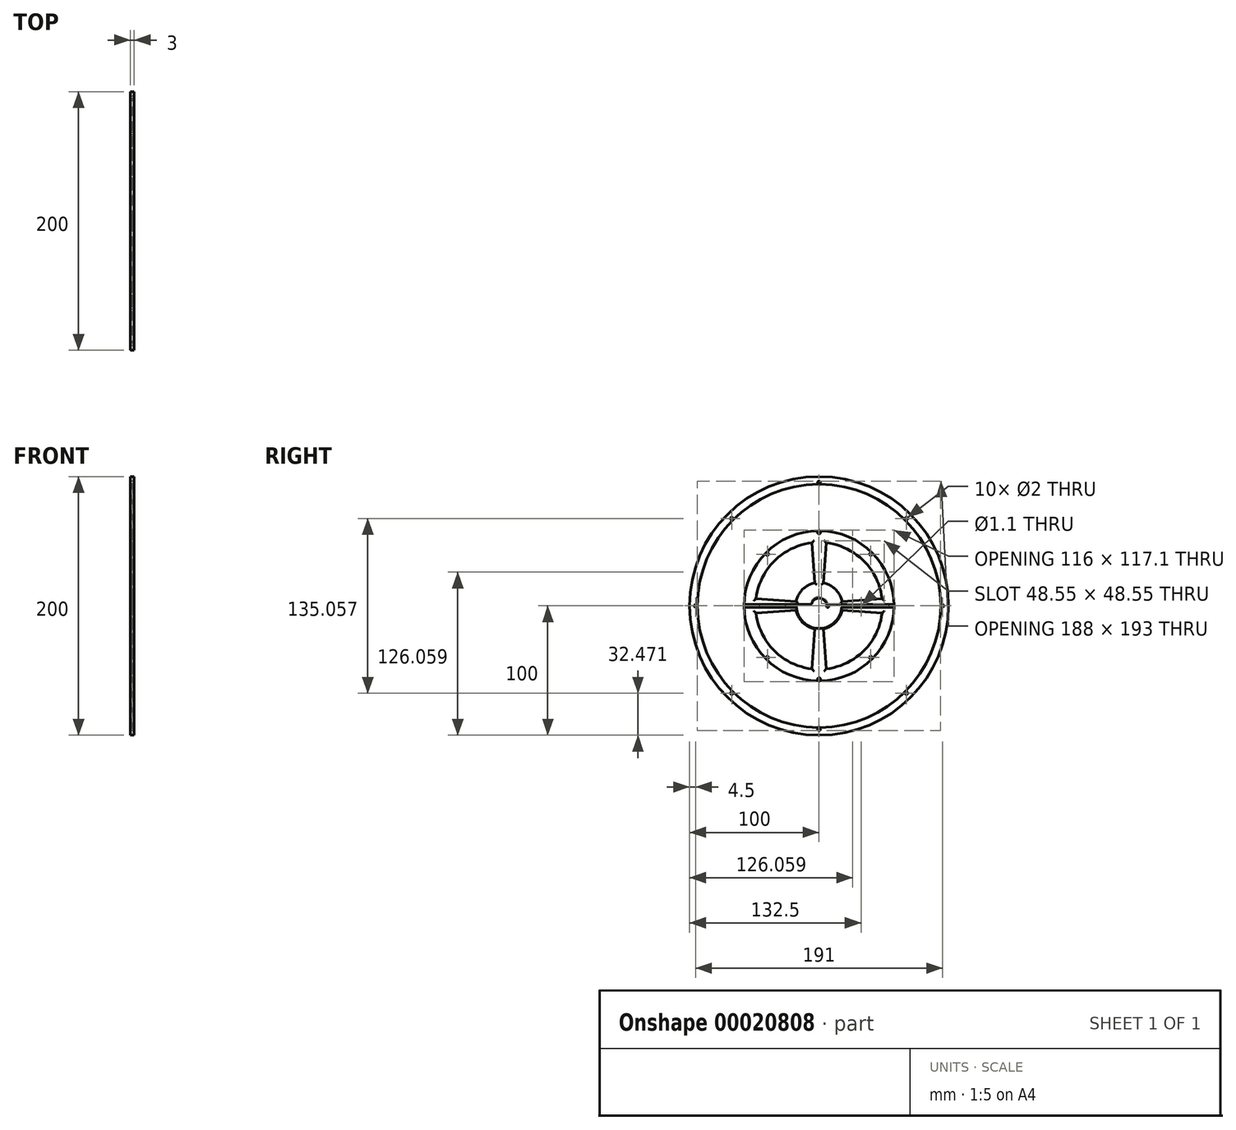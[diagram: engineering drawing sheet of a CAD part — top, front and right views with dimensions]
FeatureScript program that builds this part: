
annotation { "Feature Type Name" : "Feature", "Feature Type Description" : "" }
export const myFeature = defineFeature(function(context is Context, id is Id, definition is map)
    precondition{}
    {
        {
            var Q0;
            Q0=qCreatedBy(makeId("Right.planeOp"),FACE);
            var sketch = newSketch(context, id + "F0", { "sketchPlane" : qUnion([Q0])});
            skCircle(sketch, "E0", {"center": v(0, 0) * mm, "radius": 49 * mm});
            skCircle(sketch, "E1", {"center": v(0, 0) * mm, "radius": 58 * mm});
            skCircle(sketch, "E2", {"center": v(0, 0) * mm, "radius": 94 * mm});
            skCircle(sketch, "E3", {"center": v(0, 0) * mm, "radius": 100 * mm});
            skCircle(sketch, "E4", {"center": v(0, 0) * mm, "radius": 18 * mm});
            skCircle(sketch, "E5", {"center": v(0, 0) * mm, "radius": 6 * mm});
            skCircle(sketch, "E6", {"center": v(0, 0) * mm, "radius": 6.5 * mm});
            skCircle(sketch, "E7", {"center": v(0, 0) * mm, "radius": 7 * mm});
            skCircle(sketch, "E8.cCircle", {"center": v(0, 0) * mm, "radius": 58 * mm, "construction": true});
            skCircle(sketch, "E9", {"center": v(56.5, 0) * mm, "radius": 1 * mm});
            skCircle(sketch, "E10", {"center": v(95.5, 0) * mm, "radius": 1 * mm});
            skCircle(sketch, "E11.1.0", {"center": v(67.53, 67.53) * mm, "radius": 1 * mm});
            skCircle(sketch, "E11.1.1", {"center": v(39.95, 39.95) * mm, "radius": 1 * mm});
            skCircle(sketch, "E11.2.0", {"center": v(0, 95.5) * mm, "radius": 1 * mm});
            skCircle(sketch, "E11.2.1", {"center": v(0, 56.5) * mm, "radius": 1 * mm});
            skCircle(sketch, "E12.1.3.0", {"center": v(-67.53, 67.53) * mm, "radius": 1 * mm});
            skCircle(sketch, "E12.2.3.0", {"center": v(-39.95, 39.95) * mm, "radius": 1 * mm});
            skCircle(sketch, "E12.1.4.0", {"center": v(-95.5, 0) * mm, "radius": 1 * mm});
            skCircle(sketch, "E12.2.4.0", {"center": v(-56.5, 0) * mm, "radius": 1 * mm});
            skCircle(sketch, "E12.1.5.0", {"center": v(-67.53, -67.53) * mm, "radius": 1 * mm});
            skCircle(sketch, "E12.2.5.0", {"center": v(-39.95, -39.95) * mm, "radius": 1 * mm});
            skCircle(sketch, "E12.1.6.0", {"center": v(0, -95.5) * mm, "radius": 1 * mm});
            skCircle(sketch, "E12.2.6.0", {"center": v(0, -56.5) * mm, "radius": 1 * mm});
            skCircle(sketch, "E12.1.7.0", {"center": v(67.53, -67.53) * mm, "radius": 1 * mm});
            skCircle(sketch, "E12.2.7.0", {"center": v(39.95, -39.95) * mm, "radius": 1 * mm});
            skPoint(sketch, "E13", {"position": v(0, -58) * mm});
            skPoint(sketch, "E14", {"position": v(0, -94) * mm});
            skPoint(sketch, "E15", {"position": v(18.53, 0) * mm});
            skPoint(sketch, "E16", {"position": v(32.5, 0) * mm});
            skPoint(sketch, "E17", {"position": v(-17.5, 0) * mm});
            skPoint(sketch, "E18", {"position": v(-7.5, 0) * mm});
            skPoint(sketch, "E19", {"position": v(55, 0) * mm});
            skPoint(sketch, "E20", {"position": v(-55, 0) * mm});
            skLineSegment(sketch, "E21.rect.bottom", {"start": v(56.5, -1) * mm, "end": v(-56.5, -1) * mm});
            skLineSegment(sketch, "E21.rect.top", {"start": v(56.5, 1) * mm, "end": v(-56.5, 1) * mm});
            skLineSegment(sketch, "E21.rect.left", {"start": v(56.5, -1) * mm, "end": v(56.5, 1) * mm});
            skLineSegment(sketch, "E21.rect.right", {"start": v(-56.5, -1) * mm, "end": v(-56.5, 1) * mm});
            skPoint(sketch, "E22", {"position": v(0, 94) * mm});
            skPoint(sketch, "E23", {"position": v(0, 58) * mm});
            skCircle(sketch, "E24", {"center": v(0, 0) * mm, "radius": 56.5 * mm});
            skCircle(sketch, "E25", {"center": v(0, 0) * mm, "radius": 7.5 * mm});
            skCircle(sketch, "E26", {"center": v(0, 0) * mm, "radius": 17.5 * mm});
            skCircle(sketch, "E27", {"center": v(0, 0) * mm, "radius": 55 * mm});
            skPoint(sketch, "E28.0.midPoint", {"position": v(-58, 0) * mm});
            skLineSegment(sketch, "E29", {"start": v(5.48, 48.7) * mm, "end": v(3.37, 17.68) * mm});
            skLineSegment(sketch, "E30", {"start": v(-5.48, 48.7) * mm, "end": v(-3.37, 17.68) * mm});
            skLineSegment(sketch, "E31", {"start": v(48.7, -5.48) * mm, "end": v(17.68, -3.37) * mm});
            skLineSegment(sketch, "E32", {"start": v(48.7, 5.48) * mm, "end": v(17.68, 3.37) * mm});
            skLineSegment(sketch, "E33", {"start": v(-48.7, -5.48) * mm, "end": v(-17.68, -3.37) * mm});
            skLineSegment(sketch, "E34", {"start": v(-48.7, 5.48) * mm, "end": v(-17.68, 3.37) * mm});
            skLineSegment(sketch, "E35", {"start": v(-5.48, -48.7) * mm, "end": v(-3.37, -17.68) * mm});
            skLineSegment(sketch, "E36", {"start": v(3.37, -17.68) * mm, "end": v(5.48, -48.7) * mm});
            skSolve(sketch);
        }
        {
            var Q0;
            Q0=makeQuery(id+"F0.imprint","IMPRINT",FACE,{"disambiguationData":[TD([[makeQuery(id+"F0.imprint","IMPRINT",EDGE,{"derivedFrom":sQuery(id+"F0.wireOp",EDGE,"E2")}),-1.0]])]});
            var Q1;
            Q1=makeQuery(id+"F0.imprint","IMPRINT",FACE,{"disambiguationData":[TD([[makeQuery(id+"F0.imprint","IMPRINT",EDGE,{"derivedFrom":sQuery(id+"F0.wireOp",EDGE,"E1")}),1.0]])]});
            var Q2;
            {var subQ4=sQuery(id+"F0.wireOp",EDGE,"E24");var subQ12=sQuery(id+"F0.wireOp",EDGE,"E11.1.1");var subQ14=makeQuery(id+"F0.imprint","INTERSECT",VERTEX,{"disambiguationData":[OD(0.0)],"derivedFrom":[subQ12,subQ4]});Q2=makeQuery(id+"F0.imprint","IMPRINT",FACE,{"disambiguationData":[TD([[makeQuery(id+"F0.imprint","IMPRINT",EDGE,{"disambiguationData":[TD([[subQ14,1.0]])],"derivedFrom":subQ12}),-1.0]])]});}
            var Q3;
            {var subQ4=sQuery(id+"F0.wireOp",EDGE,"E0");var subQ10=makeQuery(id+"F0.imprint","INTERSECT",VERTEX,{"derivedFrom":[subQ4,sQuery(id+"F0.wireOp",EDGE,"E32")]});Q3=makeQuery(id+"F0.imprint","IMPRINT",FACE,{"disambiguationData":[TD([[makeQuery(id+"F0.imprint","IMPRINT",EDGE,{"disambiguationData":[TD([[subQ10,1.0]])],"derivedFrom":subQ4}),-1.0]])]});}
            var Q4;
            {var subQ4=sQuery(id+"F0.wireOp",EDGE,"E0");var subQ10=makeQuery(id+"F0.imprint","INTERSECT",VERTEX,{"derivedFrom":[subQ4,sQuery(id+"F0.wireOp",EDGE,"E33")]});Q4=makeQuery(id+"F0.imprint","IMPRINT",FACE,{"disambiguationData":[TD([[makeQuery(id+"F0.imprint","IMPRINT",EDGE,{"disambiguationData":[TD([[subQ10,1.0]])],"derivedFrom":subQ4}),-1.0]])]});}
            var Q5;
            {var subQ0=sQuery(id+"F0.wireOp",EDGE,"E34");Q5=makeQuery(id+"F0.imprint","IMPRINT",FACE,{"disambiguationData":[TD([[makeQuery(id+"F0.imprint","IMPRINT",EDGE,{"derivedFrom":subQ0}),-1.0]])]});}
            var Q6;
            {var subQ0=sQuery(id+"F0.wireOp",EDGE,"E33");Q6=makeQuery(id+"F0.imprint","IMPRINT",FACE,{"disambiguationData":[TD([[makeQuery(id+"F0.imprint","IMPRINT",EDGE,{"derivedFrom":subQ0}),1.0]])]});}
            var Q7;
            {var subQ0=sQuery(id+"F0.wireOp",EDGE,"E26");var subQ1=sQuery(id+"F0.wireOp",EDGE,"E21.rect.top");var subQ3=makeQuery(id+"F0.imprint","INTERSECT",VERTEX,{"disambiguationData":[OD(0.0)],"derivedFrom":[subQ1,subQ0]});Q7=makeQuery(id+"F0.imprint","IMPRINT",FACE,{"disambiguationData":[TD([[makeQuery(id+"F0.imprint","IMPRINT",EDGE,{"disambiguationData":[TD([[subQ3,-1.0]])],"derivedFrom":subQ1}),-1.0]])]});}
            var Q8;
            {var subQ1=sQuery(id+"F0.wireOp",EDGE,"E29");Q8=makeQuery(id+"F0.imprint","IMPRINT",FACE,{"disambiguationData":[TD([[makeQuery(id+"F0.imprint","IMPRINT",EDGE,{"derivedFrom":subQ1}),-1.0]])]});}
            var Q9;
            {var subQ0=sQuery(id+"F0.wireOp",EDGE,"E32");Q9=makeQuery(id+"F0.imprint","IMPRINT",FACE,{"disambiguationData":[TD([[makeQuery(id+"F0.imprint","IMPRINT",EDGE,{"derivedFrom":subQ0}),1.0]])]});}
            var Q10;
            {var subQ0=sQuery(id+"F0.wireOp",EDGE,"E31");Q10=makeQuery(id+"F0.imprint","IMPRINT",FACE,{"disambiguationData":[TD([[makeQuery(id+"F0.imprint","IMPRINT",EDGE,{"derivedFrom":subQ0}),-1.0]])]});}
            var Q11;
            {var subQ0=sQuery(id+"F0.wireOp",EDGE,"E26");var subQ1=sQuery(id+"F0.wireOp",EDGE,"E21.rect.bottom");var subQ3=makeQuery(id+"F0.imprint","INTERSECT",VERTEX,{"disambiguationData":[OD(0.0)],"derivedFrom":[subQ1,subQ0]});Q11=makeQuery(id+"F0.imprint","IMPRINT",FACE,{"disambiguationData":[TD([[makeQuery(id+"F0.imprint","IMPRINT",EDGE,{"disambiguationData":[TD([[subQ3,-1.0]])],"derivedFrom":subQ1}),1.0]])]});}
            var Q12;
            {var subQ1=sQuery(id+"F0.wireOp",EDGE,"E35");Q12=makeQuery(id+"F0.imprint","IMPRINT",FACE,{"disambiguationData":[TD([[makeQuery(id+"F0.imprint","IMPRINT",EDGE,{"derivedFrom":subQ1}),-1.0]])]});}
            var Q13;
            {var subQ0=sQuery(id+"F0.wireOp",EDGE,"E24");var subQ10=sQuery(id+"F0.wireOp",EDGE,"E12.2.5.0");var subQ12=makeQuery(id+"F0.imprint","INTERSECT",VERTEX,{"disambiguationData":[OD(0.0)],"derivedFrom":[subQ10,subQ0]});Q13=makeQuery(id+"F0.imprint","IMPRINT",FACE,{"disambiguationData":[TD([[makeQuery(id+"F0.imprint","IMPRINT",EDGE,{"disambiguationData":[TD([[subQ12,1.0]])],"derivedFrom":subQ10}),-1.0]])]});}
            var Q14;
            {var subQ3=sQuery(id+"F0.wireOp",EDGE,"E4");var subQ10=makeQuery(id+"F0.imprint","INTERSECT",VERTEX,{"derivedFrom":[subQ3,sQuery(id+"F0.wireOp",EDGE,"E33")]});Q14=makeQuery(id+"F0.imprint","IMPRINT",FACE,{"disambiguationData":[TD([[makeQuery(id+"F0.imprint","IMPRINT",EDGE,{"disambiguationData":[TD([[subQ10,1.0]])],"derivedFrom":subQ3}),1.0]])]});}
            var Q15;
            {var subQ1=sQuery(id+"F0.wireOp",EDGE,"E21.rect.bottom");var subQ4=sQuery(id+"F0.wireOp",EDGE,"E7");var subQ5=makeQuery(id+"F0.imprint","INTERSECT",VERTEX,{"disambiguationData":[OD(0.0)],"derivedFrom":[subQ4,subQ1]});Q15=makeQuery(id+"F0.imprint","IMPRINT",FACE,{"disambiguationData":[TD([[makeQuery(id+"F0.imprint","IMPRINT",EDGE,{"disambiguationData":[TD([[subQ5,-1.0]])],"derivedFrom":subQ4}),-1.0]])]});}
            var Q16;
            {var subQ0=sQuery(id+"F0.wireOp",EDGE,"E21.rect.bottom");var subQ3=sQuery(id+"F0.wireOp",EDGE,"E6");var subQ4=makeQuery(id+"F0.imprint","INTERSECT",VERTEX,{"disambiguationData":[OD(0.0)],"derivedFrom":[subQ3,subQ0]});Q16=makeQuery(id+"F0.imprint","IMPRINT",FACE,{"disambiguationData":[TD([[makeQuery(id+"F0.imprint","IMPRINT",EDGE,{"disambiguationData":[TD([[subQ4,-1.0]])],"derivedFrom":subQ3}),-1.0]])]});}
            var Q17;
            {var subQ0=sQuery(id+"F0.wireOp",EDGE,"E21.rect.bottom");var subQ3=sQuery(id+"F0.wireOp",EDGE,"E5");var subQ4=makeQuery(id+"F0.imprint","INTERSECT",VERTEX,{"disambiguationData":[OD(0.0)],"derivedFrom":[subQ3,subQ0]});Q17=makeQuery(id+"F0.imprint","IMPRINT",FACE,{"disambiguationData":[TD([[makeQuery(id+"F0.imprint","IMPRINT",EDGE,{"disambiguationData":[TD([[subQ4,-1.0]])],"derivedFrom":subQ3}),-1.0]])]});}
            var Q18;
            {var subQ1=sQuery(id+"F0.wireOp",EDGE,"E21.rect.top");var subQ5=sQuery(id+"F0.wireOp",EDGE,"E7");var subQ6=makeQuery(id+"F0.imprint","INTERSECT",VERTEX,{"disambiguationData":[OD(0.0)],"derivedFrom":[subQ5,subQ1]});Q18=makeQuery(id+"F0.imprint","IMPRINT",FACE,{"disambiguationData":[TD([[makeQuery(id+"F0.imprint","IMPRINT",EDGE,{"disambiguationData":[TD([[subQ6,-1.0]])],"derivedFrom":subQ5}),-1.0]])]});}
            var Q19;
            {var subQ0=sQuery(id+"F0.wireOp",EDGE,"E21.rect.top");var subQ3=sQuery(id+"F0.wireOp",EDGE,"E6");var subQ4=makeQuery(id+"F0.imprint","INTERSECT",VERTEX,{"disambiguationData":[OD(0.0)],"derivedFrom":[subQ3,subQ0]});Q19=makeQuery(id+"F0.imprint","IMPRINT",FACE,{"disambiguationData":[TD([[makeQuery(id+"F0.imprint","IMPRINT",EDGE,{"disambiguationData":[TD([[subQ4,-1.0]])],"derivedFrom":subQ3}),-1.0]])]});}
            var Q20;
            {var subQ0=sQuery(id+"F0.wireOp",EDGE,"E21.rect.top");var subQ3=sQuery(id+"F0.wireOp",EDGE,"E5");var subQ4=makeQuery(id+"F0.imprint","INTERSECT",VERTEX,{"disambiguationData":[OD(0.0)],"derivedFrom":[subQ3,subQ0]});Q20=makeQuery(id+"F0.imprint","IMPRINT",FACE,{"disambiguationData":[TD([[makeQuery(id+"F0.imprint","IMPRINT",EDGE,{"disambiguationData":[TD([[subQ4,-1.0]])],"derivedFrom":subQ3}),-1.0]])]});}
            var Q21;
            {var subQ3=sQuery(id+"F0.wireOp",EDGE,"E5");var subQ5=sQuery(id+"F0.wireOp",EDGE,"E21.rect.top");var subQ7=makeQuery(id+"F0.imprint","INTERSECT",VERTEX,{"disambiguationData":[OD(1.0)],"derivedFrom":[subQ3,subQ5]});Q21=makeQuery(id+"F0.imprint","IMPRINT",FACE,{"disambiguationData":[TD([[makeQuery(id+"F0.imprint","IMPRINT",EDGE,{"disambiguationData":[TD([[subQ7,1.0]])],"derivedFrom":subQ3}),-1.0]])]});}
            var Q22;
            {var subQ0=sQuery(id+"F0.wireOp",EDGE,"E21.rect.top");var subQ3=sQuery(id+"F0.wireOp",EDGE,"E6");var subQ4=makeQuery(id+"F0.imprint","INTERSECT",VERTEX,{"disambiguationData":[OD(1.0)],"derivedFrom":[subQ3,subQ0]});Q22=makeQuery(id+"F0.imprint","IMPRINT",FACE,{"disambiguationData":[TD([[makeQuery(id+"F0.imprint","IMPRINT",EDGE,{"disambiguationData":[TD([[subQ4,1.0]])],"derivedFrom":subQ3}),-1.0]])]});}
            var Q23;
            {var subQ1=sQuery(id+"F0.wireOp",EDGE,"E21.rect.top");var subQ5=sQuery(id+"F0.wireOp",EDGE,"E7");var subQ6=makeQuery(id+"F0.imprint","INTERSECT",VERTEX,{"disambiguationData":[OD(1.0)],"derivedFrom":[subQ5,subQ1]});Q23=makeQuery(id+"F0.imprint","IMPRINT",FACE,{"disambiguationData":[TD([[makeQuery(id+"F0.imprint","IMPRINT",EDGE,{"disambiguationData":[TD([[subQ6,1.0]])],"derivedFrom":subQ5}),-1.0]])]});}
            var Q24;
            {var subQ1=sQuery(id+"F0.wireOp",EDGE,"E21.rect.top");var subQ4=sQuery(id+"F0.wireOp",EDGE,"E7");var subQ5=makeQuery(id+"F0.imprint","INTERSECT",VERTEX,{"disambiguationData":[OD(0.0)],"derivedFrom":[subQ4,subQ1]});Q24=makeQuery(id+"F0.imprint","IMPRINT",FACE,{"disambiguationData":[TD([[makeQuery(id+"F0.imprint","IMPRINT",EDGE,{"disambiguationData":[TD([[subQ5,1.0]])],"derivedFrom":subQ4}),-1.0]])]});}
            var Q25;
            {var subQ0=sQuery(id+"F0.wireOp",EDGE,"E21.rect.top");var subQ3=sQuery(id+"F0.wireOp",EDGE,"E6");var subQ4=makeQuery(id+"F0.imprint","INTERSECT",VERTEX,{"disambiguationData":[OD(0.0)],"derivedFrom":[subQ3,subQ0]});Q25=makeQuery(id+"F0.imprint","IMPRINT",FACE,{"disambiguationData":[TD([[makeQuery(id+"F0.imprint","IMPRINT",EDGE,{"disambiguationData":[TD([[subQ4,1.0]])],"derivedFrom":subQ3}),-1.0]])]});}
            var Q26;
            {var subQ0=sQuery(id+"F0.wireOp",EDGE,"E21.rect.top");var subQ3=sQuery(id+"F0.wireOp",EDGE,"E5");var subQ4=makeQuery(id+"F0.imprint","INTERSECT",VERTEX,{"disambiguationData":[OD(0.0)],"derivedFrom":[subQ3,subQ0]});Q26=makeQuery(id+"F0.imprint","IMPRINT",FACE,{"disambiguationData":[TD([[makeQuery(id+"F0.imprint","IMPRINT",EDGE,{"disambiguationData":[TD([[subQ4,1.0]])],"derivedFrom":subQ3}),-1.0]])]});}
            var Q27;
            {var subQ3=sQuery(id+"F0.wireOp",EDGE,"E4");var subQ10=makeQuery(id+"F0.imprint","INTERSECT",VERTEX,{"derivedFrom":[subQ3,sQuery(id+"F0.wireOp",EDGE,"E32")]});Q27=makeQuery(id+"F0.imprint","IMPRINT",FACE,{"disambiguationData":[TD([[makeQuery(id+"F0.imprint","IMPRINT",EDGE,{"disambiguationData":[TD([[subQ10,1.0]])],"derivedFrom":subQ3}),1.0]])]});}
            extrude(context, id + "F1", {"entities" : qUnion([Q0, Q1, Q2, Q3, Q4, Q5, Q6, Q7, Q8, Q9, Q10, Q11, Q12, Q13, Q14, Q15, Q16, Q17, Q18, Q19, Q20, Q21, Q22, Q23, Q24, Q25, Q26, Q27]), "depth" : 1 * mm});
        }
        {
            var Q0;
            Q0=makeQuery(id+"F0.imprint","IMPRINT",FACE,{"disambiguationData":[TD([[makeQuery(id+"F0.imprint","IMPRINT",EDGE,{"derivedFrom":sQuery(id+"F0.wireOp",EDGE,"E2")}),-1.0]])]});
            var Q1;
            Q1=makeQuery(id+"F0.imprint","IMPRINT",FACE,{"disambiguationData":[TD([[makeQuery(id+"F0.imprint","IMPRINT",EDGE,{"derivedFrom":sQuery(id+"F0.wireOp",EDGE,"E1")}),-1.0]])]});
            var Q2;
            Q2=makeQuery(id+"F0.imprint","IMPRINT",FACE,{"disambiguationData":[TD([[makeQuery(id+"F0.imprint","IMPRINT",EDGE,{"derivedFrom":sQuery(id+"F0.wireOp",EDGE,"E1")}),1.0]])]});
            var Q3;
            {var subQ4=sQuery(id+"F0.wireOp",EDGE,"E24");var subQ12=sQuery(id+"F0.wireOp",EDGE,"E11.1.1");var subQ14=makeQuery(id+"F0.imprint","INTERSECT",VERTEX,{"disambiguationData":[OD(0.0)],"derivedFrom":[subQ12,subQ4]});Q3=makeQuery(id+"F0.imprint","IMPRINT",FACE,{"disambiguationData":[TD([[makeQuery(id+"F0.imprint","IMPRINT",EDGE,{"disambiguationData":[TD([[subQ14,1.0]])],"derivedFrom":subQ12}),-1.0]])]});}
            var Q4;
            {var subQ4=sQuery(id+"F0.wireOp",EDGE,"E0");var subQ10=makeQuery(id+"F0.imprint","INTERSECT",VERTEX,{"derivedFrom":[subQ4,sQuery(id+"F0.wireOp",EDGE,"E32")]});Q4=makeQuery(id+"F0.imprint","IMPRINT",FACE,{"disambiguationData":[TD([[makeQuery(id+"F0.imprint","IMPRINT",EDGE,{"disambiguationData":[TD([[subQ10,1.0]])],"derivedFrom":subQ4}),-1.0]])]});}
            var Q5;
            {var subQ4=sQuery(id+"F0.wireOp",EDGE,"E0");var subQ10=makeQuery(id+"F0.imprint","INTERSECT",VERTEX,{"derivedFrom":[subQ4,sQuery(id+"F0.wireOp",EDGE,"E33")]});Q5=makeQuery(id+"F0.imprint","IMPRINT",FACE,{"disambiguationData":[TD([[makeQuery(id+"F0.imprint","IMPRINT",EDGE,{"disambiguationData":[TD([[subQ10,1.0]])],"derivedFrom":subQ4}),-1.0]])]});}
            var Q6;
            {var subQ0=sQuery(id+"F0.wireOp",EDGE,"E24");var subQ10=sQuery(id+"F0.wireOp",EDGE,"E12.2.5.0");var subQ12=makeQuery(id+"F0.imprint","INTERSECT",VERTEX,{"disambiguationData":[OD(0.0)],"derivedFrom":[subQ10,subQ0]});Q6=makeQuery(id+"F0.imprint","IMPRINT",FACE,{"disambiguationData":[TD([[makeQuery(id+"F0.imprint","IMPRINT",EDGE,{"disambiguationData":[TD([[subQ12,1.0]])],"derivedFrom":subQ10}),-1.0]])]});}
            var Q7;
            {var subQ1=sQuery(id+"F0.wireOp",EDGE,"E21.rect.top");var subQ5=sQuery(id+"F0.wireOp",EDGE,"E0");var subQ6=makeQuery(id+"F0.imprint","INTERSECT",VERTEX,{"disambiguationData":[OD(1.0)],"derivedFrom":[subQ5,subQ1]});Q7=makeQuery(id+"F0.imprint","IMPRINT",FACE,{"disambiguationData":[TD([[makeQuery(id+"F0.imprint","IMPRINT",EDGE,{"disambiguationData":[TD([[subQ6,-1.0]])],"derivedFrom":subQ5}),-1.0]])]});}
            var Q8;
            {var subQ0=sQuery(id+"F0.wireOp",EDGE,"E34");Q8=makeQuery(id+"F0.imprint","IMPRINT",FACE,{"disambiguationData":[TD([[makeQuery(id+"F0.imprint","IMPRINT",EDGE,{"derivedFrom":subQ0}),-1.0]])]});}
            var Q9;
            {var subQ0=sQuery(id+"F0.wireOp",EDGE,"E33");Q9=makeQuery(id+"F0.imprint","IMPRINT",FACE,{"disambiguationData":[TD([[makeQuery(id+"F0.imprint","IMPRINT",EDGE,{"derivedFrom":subQ0}),1.0]])]});}
            var Q10;
            {var subQ0=sQuery(id+"F0.wireOp",EDGE,"E26");var subQ1=sQuery(id+"F0.wireOp",EDGE,"E21.rect.top");var subQ3=makeQuery(id+"F0.imprint","INTERSECT",VERTEX,{"disambiguationData":[OD(0.0)],"derivedFrom":[subQ1,subQ0]});Q10=makeQuery(id+"F0.imprint","IMPRINT",FACE,{"disambiguationData":[TD([[makeQuery(id+"F0.imprint","IMPRINT",EDGE,{"disambiguationData":[TD([[subQ3,-1.0]])],"derivedFrom":subQ1}),-1.0]])]});}
            var Q11;
            {var subQ0=sQuery(id+"F0.wireOp",EDGE,"E26");var subQ1=sQuery(id+"F0.wireOp",EDGE,"E21.rect.bottom");var subQ3=makeQuery(id+"F0.imprint","INTERSECT",VERTEX,{"disambiguationData":[OD(0.0)],"derivedFrom":[subQ1,subQ0]});Q11=makeQuery(id+"F0.imprint","IMPRINT",FACE,{"disambiguationData":[TD([[makeQuery(id+"F0.imprint","IMPRINT",EDGE,{"disambiguationData":[TD([[subQ3,-1.0]])],"derivedFrom":subQ1}),1.0]])]});}
            var Q12;
            {var subQ1=sQuery(id+"F0.wireOp",EDGE,"E29");Q12=makeQuery(id+"F0.imprint","IMPRINT",FACE,{"disambiguationData":[TD([[makeQuery(id+"F0.imprint","IMPRINT",EDGE,{"derivedFrom":subQ1}),-1.0]])]});}
            var Q13;
            {var subQ0=sQuery(id+"F0.wireOp",EDGE,"E21.rect.top");var subQ3=sQuery(id+"F0.wireOp",EDGE,"E0");var subQ4=makeQuery(id+"F0.imprint","INTERSECT",VERTEX,{"disambiguationData":[OD(0.0)],"derivedFrom":[subQ3,subQ0]});Q13=makeQuery(id+"F0.imprint","IMPRINT",FACE,{"disambiguationData":[TD([[makeQuery(id+"F0.imprint","IMPRINT",EDGE,{"disambiguationData":[TD([[subQ4,1.0]])],"derivedFrom":subQ3}),1.0]])]});}
            var Q14;
            {var subQ0=sQuery(id+"F0.wireOp",EDGE,"E31");Q14=makeQuery(id+"F0.imprint","IMPRINT",FACE,{"disambiguationData":[TD([[makeQuery(id+"F0.imprint","IMPRINT",EDGE,{"derivedFrom":subQ0}),-1.0]])]});}
            var Q15;
            {var subQ0=sQuery(id+"F0.wireOp",EDGE,"E26");var subQ3=sQuery(id+"F0.wireOp",EDGE,"E21.rect.bottom");var subQ4=makeQuery(id+"F0.imprint","INTERSECT",VERTEX,{"disambiguationData":[OD(0.0)],"derivedFrom":[subQ3,subQ0]});Q15=makeQuery(id+"F0.imprint","IMPRINT",FACE,{"disambiguationData":[TD([[makeQuery(id+"F0.imprint","IMPRINT",EDGE,{"disambiguationData":[TD([[subQ4,-1.0]])],"derivedFrom":subQ3}),-1.0]])]});}
            var Q16;
            {var subQ3=sQuery(id+"F0.wireOp",EDGE,"E21.rect.bottom");var subQ5=sQuery(id+"F0.wireOp",EDGE,"E25");var subQ7=makeQuery(id+"F0.imprint","INTERSECT",VERTEX,{"disambiguationData":[OD(1.0)],"derivedFrom":[subQ3,subQ5]});Q16=makeQuery(id+"F0.imprint","IMPRINT",FACE,{"disambiguationData":[TD([[makeQuery(id+"F0.imprint","IMPRINT",EDGE,{"disambiguationData":[TD([[subQ7,-1.0]])],"derivedFrom":subQ3}),-1.0]])]});}
            var Q17;
            {var subQ0=sQuery(id+"F0.wireOp",EDGE,"E21.rect.top");var subQ3=sQuery(id+"F0.wireOp",EDGE,"E0");var subQ4=makeQuery(id+"F0.imprint","INTERSECT",VERTEX,{"disambiguationData":[OD(1.0)],"derivedFrom":[subQ3,subQ0]});Q17=makeQuery(id+"F0.imprint","IMPRINT",FACE,{"disambiguationData":[TD([[makeQuery(id+"F0.imprint","IMPRINT",EDGE,{"disambiguationData":[TD([[subQ4,-1.0]])],"derivedFrom":subQ3}),1.0]])]});}
            var Q18;
            {var subQ0=sQuery(id+"F0.wireOp",EDGE,"E32");Q18=makeQuery(id+"F0.imprint","IMPRINT",FACE,{"disambiguationData":[TD([[makeQuery(id+"F0.imprint","IMPRINT",EDGE,{"derivedFrom":subQ0}),1.0]])]});}
            var Q19;
            {var subQ1=sQuery(id+"F0.wireOp",EDGE,"E35");Q19=makeQuery(id+"F0.imprint","IMPRINT",FACE,{"disambiguationData":[TD([[makeQuery(id+"F0.imprint","IMPRINT",EDGE,{"derivedFrom":subQ1}),-1.0]])]});}
            var Q20;
            {var subQ3=sQuery(id+"F0.wireOp",EDGE,"E4");var subQ10=makeQuery(id+"F0.imprint","INTERSECT",VERTEX,{"derivedFrom":[subQ3,sQuery(id+"F0.wireOp",EDGE,"E32")]});Q20=makeQuery(id+"F0.imprint","IMPRINT",FACE,{"disambiguationData":[TD([[makeQuery(id+"F0.imprint","IMPRINT",EDGE,{"disambiguationData":[TD([[subQ10,1.0]])],"derivedFrom":subQ3}),1.0]])]});}
            var Q21;
            {var subQ1=sQuery(id+"F0.wireOp",EDGE,"E21.rect.top");var subQ5=sQuery(id+"F0.wireOp",EDGE,"E4");var subQ6=makeQuery(id+"F0.imprint","INTERSECT",VERTEX,{"disambiguationData":[OD(1.0)],"derivedFrom":[subQ5,subQ1]});Q21=makeQuery(id+"F0.imprint","IMPRINT",FACE,{"disambiguationData":[TD([[makeQuery(id+"F0.imprint","IMPRINT",EDGE,{"disambiguationData":[TD([[subQ6,-1.0]])],"derivedFrom":subQ5}),1.0]])]});}
            var Q22;
            {var subQ3=sQuery(id+"F0.wireOp",EDGE,"E4");var subQ10=makeQuery(id+"F0.imprint","INTERSECT",VERTEX,{"derivedFrom":[subQ3,sQuery(id+"F0.wireOp",EDGE,"E33")]});Q22=makeQuery(id+"F0.imprint","IMPRINT",FACE,{"disambiguationData":[TD([[makeQuery(id+"F0.imprint","IMPRINT",EDGE,{"disambiguationData":[TD([[subQ10,1.0]])],"derivedFrom":subQ3}),1.0]])]});}
            var Q23;
            {var subQ0=sQuery(id+"F0.wireOp",EDGE,"E21.rect.top");var subQ3=sQuery(id+"F0.wireOp",EDGE,"E5");var subQ4=makeQuery(id+"F0.imprint","INTERSECT",VERTEX,{"disambiguationData":[OD(0.0)],"derivedFrom":[subQ3,subQ0]});Q23=makeQuery(id+"F0.imprint","IMPRINT",FACE,{"disambiguationData":[TD([[makeQuery(id+"F0.imprint","IMPRINT",EDGE,{"disambiguationData":[TD([[subQ4,-1.0]])],"derivedFrom":subQ3}),-1.0]])]});}
            var Q24;
            {var subQ1=sQuery(id+"F0.wireOp",EDGE,"E21.rect.top");var subQ5=sQuery(id+"F0.wireOp",EDGE,"E7");var subQ6=makeQuery(id+"F0.imprint","INTERSECT",VERTEX,{"disambiguationData":[OD(0.0)],"derivedFrom":[subQ5,subQ1]});Q24=makeQuery(id+"F0.imprint","IMPRINT",FACE,{"disambiguationData":[TD([[makeQuery(id+"F0.imprint","IMPRINT",EDGE,{"disambiguationData":[TD([[subQ6,-1.0]])],"derivedFrom":subQ5}),-1.0]])]});}
            var Q25;
            {var subQ1=sQuery(id+"F0.wireOp",EDGE,"E21.rect.top");var subQ4=sQuery(id+"F0.wireOp",EDGE,"E7");var subQ5=makeQuery(id+"F0.imprint","INTERSECT",VERTEX,{"disambiguationData":[OD(0.0)],"derivedFrom":[subQ4,subQ1]});Q25=makeQuery(id+"F0.imprint","IMPRINT",FACE,{"disambiguationData":[TD([[makeQuery(id+"F0.imprint","IMPRINT",EDGE,{"disambiguationData":[TD([[subQ5,1.0]])],"derivedFrom":subQ4}),-1.0]])]});}
            var Q26;
            {var subQ0=sQuery(id+"F0.wireOp",EDGE,"E21.rect.top");var subQ3=sQuery(id+"F0.wireOp",EDGE,"E5");var subQ4=makeQuery(id+"F0.imprint","INTERSECT",VERTEX,{"disambiguationData":[OD(0.0)],"derivedFrom":[subQ3,subQ0]});Q26=makeQuery(id+"F0.imprint","IMPRINT",FACE,{"disambiguationData":[TD([[makeQuery(id+"F0.imprint","IMPRINT",EDGE,{"disambiguationData":[TD([[subQ4,1.0]])],"derivedFrom":subQ3}),-1.0]])]});}
            var Q27;
            {var subQ1=sQuery(id+"F0.wireOp",EDGE,"E21.rect.bottom");var subQ4=sQuery(id+"F0.wireOp",EDGE,"E7");var subQ5=makeQuery(id+"F0.imprint","INTERSECT",VERTEX,{"disambiguationData":[OD(0.0)],"derivedFrom":[subQ4,subQ1]});Q27=makeQuery(id+"F0.imprint","IMPRINT",FACE,{"disambiguationData":[TD([[makeQuery(id+"F0.imprint","IMPRINT",EDGE,{"disambiguationData":[TD([[subQ5,-1.0]])],"derivedFrom":subQ4}),-1.0]])]});}
            var Q28;
            {var subQ0=sQuery(id+"F0.wireOp",EDGE,"E21.rect.bottom");var subQ3=sQuery(id+"F0.wireOp",EDGE,"E5");var subQ4=makeQuery(id+"F0.imprint","INTERSECT",VERTEX,{"disambiguationData":[OD(0.0)],"derivedFrom":[subQ3,subQ0]});Q28=makeQuery(id+"F0.imprint","IMPRINT",FACE,{"disambiguationData":[TD([[makeQuery(id+"F0.imprint","IMPRINT",EDGE,{"disambiguationData":[TD([[subQ4,-1.0]])],"derivedFrom":subQ3}),-1.0]])]});}
            var Q29;
            {var subQ1=sQuery(id+"F0.wireOp",EDGE,"E21.rect.top");var subQ5=sQuery(id+"F0.wireOp",EDGE,"E0");var subQ6=makeQuery(id+"F0.imprint","INTERSECT",VERTEX,{"disambiguationData":[OD(0.0)],"derivedFrom":[subQ5,subQ1]});Q29=makeQuery(id+"F0.imprint","IMPRINT",FACE,{"disambiguationData":[TD([[makeQuery(id+"F0.imprint","IMPRINT",EDGE,{"disambiguationData":[TD([[subQ6,1.0]])],"derivedFrom":subQ5}),-1.0]])]});}
            var Q30;
            {var subQ3=sQuery(id+"F0.wireOp",EDGE,"E5");var subQ5=sQuery(id+"F0.wireOp",EDGE,"E21.rect.top");var subQ7=makeQuery(id+"F0.imprint","INTERSECT",VERTEX,{"disambiguationData":[OD(1.0)],"derivedFrom":[subQ3,subQ5]});Q30=makeQuery(id+"F0.imprint","IMPRINT",FACE,{"disambiguationData":[TD([[makeQuery(id+"F0.imprint","IMPRINT",EDGE,{"disambiguationData":[TD([[subQ7,1.0]])],"derivedFrom":subQ3}),-1.0]])]});}
            var Q31;
            {var subQ1=sQuery(id+"F0.wireOp",EDGE,"E21.rect.top");var subQ5=sQuery(id+"F0.wireOp",EDGE,"E7");var subQ6=makeQuery(id+"F0.imprint","INTERSECT",VERTEX,{"disambiguationData":[OD(1.0)],"derivedFrom":[subQ5,subQ1]});Q31=makeQuery(id+"F0.imprint","IMPRINT",FACE,{"disambiguationData":[TD([[makeQuery(id+"F0.imprint","IMPRINT",EDGE,{"disambiguationData":[TD([[subQ6,1.0]])],"derivedFrom":subQ5}),-1.0]])]});}
            var Q32;
            {var subQ1=sQuery(id+"F0.wireOp",EDGE,"E21.rect.top");var subQ5=sQuery(id+"F0.wireOp",EDGE,"E4");var subQ7=makeQuery(id+"F0.imprint","INTERSECT",VERTEX,{"disambiguationData":[OD(0.0)],"derivedFrom":[subQ5,subQ1]});Q32=makeQuery(id+"F0.imprint","IMPRINT",FACE,{"disambiguationData":[TD([[makeQuery(id+"F0.imprint","IMPRINT",EDGE,{"disambiguationData":[TD([[subQ7,1.0]])],"derivedFrom":subQ5}),1.0]])]});}
            var Q33;
            {var subQ0=sQuery(id+"F0.wireOp",EDGE,"E27");var subQ3=sQuery(id+"F0.wireOp",EDGE,"E21.rect.bottom");var subQ4=makeQuery(id+"F0.imprint","INTERSECT",VERTEX,{"disambiguationData":[OD(1.0)],"derivedFrom":[subQ3,subQ0]});Q33=makeQuery(id+"F0.imprint","IMPRINT",FACE,{"disambiguationData":[TD([[makeQuery(id+"F0.imprint","IMPRINT",EDGE,{"disambiguationData":[TD([[subQ4,1.0]])],"derivedFrom":subQ0}),-1.0]])]});}
            var Q34;
            {var subQ0=sQuery(id+"F0.wireOp",EDGE,"E27");var subQ3=sQuery(id+"F0.wireOp",EDGE,"E21.rect.bottom");var subQ4=makeQuery(id+"F0.imprint","INTERSECT",VERTEX,{"disambiguationData":[OD(0.0)],"derivedFrom":[subQ3,subQ0]});Q34=makeQuery(id+"F0.imprint","IMPRINT",FACE,{"disambiguationData":[TD([[makeQuery(id+"F0.imprint","IMPRINT",EDGE,{"disambiguationData":[TD([[subQ4,-1.0]])],"derivedFrom":subQ0}),-1.0]])]});}
            extrude(context, id + "F2", {"entities" : qUnion([Q0, Q1, Q2, Q3, Q4, Q5, Q6, Q7, Q8, Q9, Q10, Q11, Q12, Q13, Q14, Q15, Q16, Q17, Q18, Q19, Q20, Q21, Q22, Q23, Q24, Q25, Q26, Q27, Q28, Q29, Q30, Q31, Q32, Q33, Q34]), "operationType" : NewBodyOperationType.ADD, "oppositeDirection" : true, "depth" : 1 * mm});
        }
        {
            var Q0;
            Q0=makeQuery(id+"F0.imprint","IMPRINT",FACE,{"disambiguationData":[TD([[makeQuery(id+"F0.imprint","IMPRINT",EDGE,{"derivedFrom":sQuery(id+"F0.wireOp",EDGE,"E2")}),-1.0]])]});
            var Q1;
            Q1=makeQuery(id+"F0.imprint","IMPRINT",FACE,{"disambiguationData":[TD([[makeQuery(id+"F0.imprint","IMPRINT",EDGE,{"derivedFrom":sQuery(id+"F0.wireOp",EDGE,"E1")}),1.0]])]});
            var Q2;
            {var subQ4=sQuery(id+"F0.wireOp",EDGE,"E24");var subQ12=sQuery(id+"F0.wireOp",EDGE,"E11.1.1");var subQ14=makeQuery(id+"F0.imprint","INTERSECT",VERTEX,{"disambiguationData":[OD(0.0)],"derivedFrom":[subQ12,subQ4]});Q2=makeQuery(id+"F0.imprint","IMPRINT",FACE,{"disambiguationData":[TD([[makeQuery(id+"F0.imprint","IMPRINT",EDGE,{"disambiguationData":[TD([[subQ14,1.0]])],"derivedFrom":subQ12}),-1.0]])]});}
            var Q3;
            {var subQ4=sQuery(id+"F0.wireOp",EDGE,"E0");var subQ10=makeQuery(id+"F0.imprint","INTERSECT",VERTEX,{"derivedFrom":[subQ4,sQuery(id+"F0.wireOp",EDGE,"E32")]});Q3=makeQuery(id+"F0.imprint","IMPRINT",FACE,{"disambiguationData":[TD([[makeQuery(id+"F0.imprint","IMPRINT",EDGE,{"disambiguationData":[TD([[subQ10,1.0]])],"derivedFrom":subQ4}),-1.0]])]});}
            var Q4;
            {var subQ0=sQuery(id+"F0.wireOp",EDGE,"E34");Q4=makeQuery(id+"F0.imprint","IMPRINT",FACE,{"disambiguationData":[TD([[makeQuery(id+"F0.imprint","IMPRINT",EDGE,{"derivedFrom":subQ0}),-1.0]])]});}
            var Q5;
            {var subQ0=sQuery(id+"F0.wireOp",EDGE,"E26");var subQ1=sQuery(id+"F0.wireOp",EDGE,"E21.rect.top");var subQ3=makeQuery(id+"F0.imprint","INTERSECT",VERTEX,{"disambiguationData":[OD(0.0)],"derivedFrom":[subQ1,subQ0]});Q5=makeQuery(id+"F0.imprint","IMPRINT",FACE,{"disambiguationData":[TD([[makeQuery(id+"F0.imprint","IMPRINT",EDGE,{"disambiguationData":[TD([[subQ3,-1.0]])],"derivedFrom":subQ1}),-1.0]])]});}
            var Q6;
            {var subQ1=sQuery(id+"F0.wireOp",EDGE,"E29");Q6=makeQuery(id+"F0.imprint","IMPRINT",FACE,{"disambiguationData":[TD([[makeQuery(id+"F0.imprint","IMPRINT",EDGE,{"derivedFrom":subQ1}),-1.0]])]});}
            var Q7;
            {var subQ4=sQuery(id+"F0.wireOp",EDGE,"E0");var subQ10=makeQuery(id+"F0.imprint","INTERSECT",VERTEX,{"derivedFrom":[subQ4,sQuery(id+"F0.wireOp",EDGE,"E33")]});Q7=makeQuery(id+"F0.imprint","IMPRINT",FACE,{"disambiguationData":[TD([[makeQuery(id+"F0.imprint","IMPRINT",EDGE,{"disambiguationData":[TD([[subQ10,1.0]])],"derivedFrom":subQ4}),-1.0]])]});}
            var Q8;
            {var subQ0=sQuery(id+"F0.wireOp",EDGE,"E33");Q8=makeQuery(id+"F0.imprint","IMPRINT",FACE,{"disambiguationData":[TD([[makeQuery(id+"F0.imprint","IMPRINT",EDGE,{"derivedFrom":subQ0}),1.0]])]});}
            var Q9;
            {var subQ0=sQuery(id+"F0.wireOp",EDGE,"E21.rect.top");var subQ3=sQuery(id+"F0.wireOp",EDGE,"E0");var subQ4=makeQuery(id+"F0.imprint","INTERSECT",VERTEX,{"disambiguationData":[OD(1.0)],"derivedFrom":[subQ3,subQ0]});Q9=makeQuery(id+"F0.imprint","IMPRINT",FACE,{"disambiguationData":[TD([[makeQuery(id+"F0.imprint","IMPRINT",EDGE,{"disambiguationData":[TD([[subQ4,-1.0]])],"derivedFrom":subQ3}),1.0]])]});}
            var Q10;
            {var subQ1=sQuery(id+"F0.wireOp",EDGE,"E21.rect.top");var subQ5=sQuery(id+"F0.wireOp",EDGE,"E0");var subQ6=makeQuery(id+"F0.imprint","INTERSECT",VERTEX,{"disambiguationData":[OD(1.0)],"derivedFrom":[subQ5,subQ1]});Q10=makeQuery(id+"F0.imprint","IMPRINT",FACE,{"disambiguationData":[TD([[makeQuery(id+"F0.imprint","IMPRINT",EDGE,{"disambiguationData":[TD([[subQ6,-1.0]])],"derivedFrom":subQ5}),-1.0]])]});}
            var Q11;
            {var subQ0=sQuery(id+"F0.wireOp",EDGE,"E24");var subQ10=sQuery(id+"F0.wireOp",EDGE,"E12.2.5.0");var subQ12=makeQuery(id+"F0.imprint","INTERSECT",VERTEX,{"disambiguationData":[OD(0.0)],"derivedFrom":[subQ10,subQ0]});Q11=makeQuery(id+"F0.imprint","IMPRINT",FACE,{"disambiguationData":[TD([[makeQuery(id+"F0.imprint","IMPRINT",EDGE,{"disambiguationData":[TD([[subQ12,1.0]])],"derivedFrom":subQ10}),-1.0]])]});}
            var Q12;
            {var subQ0=sQuery(id+"F0.wireOp",EDGE,"E26");var subQ1=sQuery(id+"F0.wireOp",EDGE,"E21.rect.bottom");var subQ3=makeQuery(id+"F0.imprint","INTERSECT",VERTEX,{"disambiguationData":[OD(0.0)],"derivedFrom":[subQ1,subQ0]});Q12=makeQuery(id+"F0.imprint","IMPRINT",FACE,{"disambiguationData":[TD([[makeQuery(id+"F0.imprint","IMPRINT",EDGE,{"disambiguationData":[TD([[subQ3,-1.0]])],"derivedFrom":subQ1}),1.0]])]});}
            var Q13;
            {var subQ3=sQuery(id+"F0.wireOp",EDGE,"E21.rect.bottom");var subQ5=sQuery(id+"F0.wireOp",EDGE,"E25");var subQ7=makeQuery(id+"F0.imprint","INTERSECT",VERTEX,{"disambiguationData":[OD(1.0)],"derivedFrom":[subQ3,subQ5]});Q13=makeQuery(id+"F0.imprint","IMPRINT",FACE,{"disambiguationData":[TD([[makeQuery(id+"F0.imprint","IMPRINT",EDGE,{"disambiguationData":[TD([[subQ7,-1.0]])],"derivedFrom":subQ3}),-1.0]])]});}
            var Q14;
            {var subQ0=sQuery(id+"F0.wireOp",EDGE,"E27");var subQ3=sQuery(id+"F0.wireOp",EDGE,"E21.rect.bottom");var subQ4=makeQuery(id+"F0.imprint","INTERSECT",VERTEX,{"disambiguationData":[OD(1.0)],"derivedFrom":[subQ3,subQ0]});Q14=makeQuery(id+"F0.imprint","IMPRINT",FACE,{"disambiguationData":[TD([[makeQuery(id+"F0.imprint","IMPRINT",EDGE,{"disambiguationData":[TD([[subQ4,1.0]])],"derivedFrom":subQ0}),-1.0]])]});}
            var Q15;
            {var subQ1=sQuery(id+"F0.wireOp",EDGE,"E35");Q15=makeQuery(id+"F0.imprint","IMPRINT",FACE,{"disambiguationData":[TD([[makeQuery(id+"F0.imprint","IMPRINT",EDGE,{"derivedFrom":subQ1}),-1.0]])]});}
            var Q16;
            {var subQ0=sQuery(id+"F0.wireOp",EDGE,"E32");Q16=makeQuery(id+"F0.imprint","IMPRINT",FACE,{"disambiguationData":[TD([[makeQuery(id+"F0.imprint","IMPRINT",EDGE,{"derivedFrom":subQ0}),1.0]])]});}
            var Q17;
            {var subQ0=sQuery(id+"F0.wireOp",EDGE,"E31");Q17=makeQuery(id+"F0.imprint","IMPRINT",FACE,{"disambiguationData":[TD([[makeQuery(id+"F0.imprint","IMPRINT",EDGE,{"derivedFrom":subQ0}),-1.0]])]});}
            var Q18;
            {var subQ0=sQuery(id+"F0.wireOp",EDGE,"E26");var subQ3=sQuery(id+"F0.wireOp",EDGE,"E21.rect.bottom");var subQ4=makeQuery(id+"F0.imprint","INTERSECT",VERTEX,{"disambiguationData":[OD(0.0)],"derivedFrom":[subQ3,subQ0]});Q18=makeQuery(id+"F0.imprint","IMPRINT",FACE,{"disambiguationData":[TD([[makeQuery(id+"F0.imprint","IMPRINT",EDGE,{"disambiguationData":[TD([[subQ4,-1.0]])],"derivedFrom":subQ3}),-1.0]])]});}
            var Q19;
            {var subQ0=sQuery(id+"F0.wireOp",EDGE,"E21.rect.top");var subQ3=sQuery(id+"F0.wireOp",EDGE,"E0");var subQ4=makeQuery(id+"F0.imprint","INTERSECT",VERTEX,{"disambiguationData":[OD(0.0)],"derivedFrom":[subQ3,subQ0]});Q19=makeQuery(id+"F0.imprint","IMPRINT",FACE,{"disambiguationData":[TD([[makeQuery(id+"F0.imprint","IMPRINT",EDGE,{"disambiguationData":[TD([[subQ4,1.0]])],"derivedFrom":subQ3}),1.0]])]});}
            var Q20;
            {var subQ1=sQuery(id+"F0.wireOp",EDGE,"E21.rect.top");var subQ5=sQuery(id+"F0.wireOp",EDGE,"E0");var subQ6=makeQuery(id+"F0.imprint","INTERSECT",VERTEX,{"disambiguationData":[OD(0.0)],"derivedFrom":[subQ5,subQ1]});Q20=makeQuery(id+"F0.imprint","IMPRINT",FACE,{"disambiguationData":[TD([[makeQuery(id+"F0.imprint","IMPRINT",EDGE,{"disambiguationData":[TD([[subQ6,1.0]])],"derivedFrom":subQ5}),-1.0]])]});}
            var Q21;
            {var subQ0=sQuery(id+"F0.wireOp",EDGE,"E27");var subQ3=sQuery(id+"F0.wireOp",EDGE,"E21.rect.bottom");var subQ4=makeQuery(id+"F0.imprint","INTERSECT",VERTEX,{"disambiguationData":[OD(0.0)],"derivedFrom":[subQ3,subQ0]});Q21=makeQuery(id+"F0.imprint","IMPRINT",FACE,{"disambiguationData":[TD([[makeQuery(id+"F0.imprint","IMPRINT",EDGE,{"disambiguationData":[TD([[subQ4,-1.0]])],"derivedFrom":subQ0}),-1.0]])]});}
            var Q22;
            {var subQ1=sQuery(id+"F0.wireOp",EDGE,"E21.rect.top");var subQ5=sQuery(id+"F0.wireOp",EDGE,"E4");var subQ6=makeQuery(id+"F0.imprint","INTERSECT",VERTEX,{"disambiguationData":[OD(1.0)],"derivedFrom":[subQ5,subQ1]});Q22=makeQuery(id+"F0.imprint","IMPRINT",FACE,{"disambiguationData":[TD([[makeQuery(id+"F0.imprint","IMPRINT",EDGE,{"disambiguationData":[TD([[subQ6,-1.0]])],"derivedFrom":subQ5}),1.0]])]});}
            var Q23;
            {var subQ3=sQuery(id+"F0.wireOp",EDGE,"E4");var subQ10=makeQuery(id+"F0.imprint","INTERSECT",VERTEX,{"derivedFrom":[subQ3,sQuery(id+"F0.wireOp",EDGE,"E32")]});Q23=makeQuery(id+"F0.imprint","IMPRINT",FACE,{"disambiguationData":[TD([[makeQuery(id+"F0.imprint","IMPRINT",EDGE,{"disambiguationData":[TD([[subQ10,1.0]])],"derivedFrom":subQ3}),1.0]])]});}
            var Q24;
            {var subQ1=sQuery(id+"F0.wireOp",EDGE,"E21.rect.top");var subQ4=sQuery(id+"F0.wireOp",EDGE,"E7");var subQ5=makeQuery(id+"F0.imprint","INTERSECT",VERTEX,{"disambiguationData":[OD(0.0)],"derivedFrom":[subQ4,subQ1]});Q24=makeQuery(id+"F0.imprint","IMPRINT",FACE,{"disambiguationData":[TD([[makeQuery(id+"F0.imprint","IMPRINT",EDGE,{"disambiguationData":[TD([[subQ5,1.0]])],"derivedFrom":subQ4}),-1.0]])]});}
            var Q25;
            {var subQ1=sQuery(id+"F0.wireOp",EDGE,"E21.rect.bottom");var subQ4=sQuery(id+"F0.wireOp",EDGE,"E7");var subQ5=makeQuery(id+"F0.imprint","INTERSECT",VERTEX,{"disambiguationData":[OD(0.0)],"derivedFrom":[subQ4,subQ1]});Q25=makeQuery(id+"F0.imprint","IMPRINT",FACE,{"disambiguationData":[TD([[makeQuery(id+"F0.imprint","IMPRINT",EDGE,{"disambiguationData":[TD([[subQ5,-1.0]])],"derivedFrom":subQ4}),-1.0]])]});}
            var Q26;
            {var subQ0=sQuery(id+"F0.wireOp",EDGE,"E21.rect.bottom");var subQ3=sQuery(id+"F0.wireOp",EDGE,"E5");var subQ4=makeQuery(id+"F0.imprint","INTERSECT",VERTEX,{"disambiguationData":[OD(0.0)],"derivedFrom":[subQ3,subQ0]});Q26=makeQuery(id+"F0.imprint","IMPRINT",FACE,{"disambiguationData":[TD([[makeQuery(id+"F0.imprint","IMPRINT",EDGE,{"disambiguationData":[TD([[subQ4,-1.0]])],"derivedFrom":subQ3}),-1.0]])]});}
            var Q27;
            {var subQ0=sQuery(id+"F0.wireOp",EDGE,"E21.rect.top");var subQ3=sQuery(id+"F0.wireOp",EDGE,"E5");var subQ4=makeQuery(id+"F0.imprint","INTERSECT",VERTEX,{"disambiguationData":[OD(0.0)],"derivedFrom":[subQ3,subQ0]});Q27=makeQuery(id+"F0.imprint","IMPRINT",FACE,{"disambiguationData":[TD([[makeQuery(id+"F0.imprint","IMPRINT",EDGE,{"disambiguationData":[TD([[subQ4,1.0]])],"derivedFrom":subQ3}),-1.0]])]});}
            var Q28;
            {var subQ0=sQuery(id+"F0.wireOp",EDGE,"E21.rect.top");var subQ3=sQuery(id+"F0.wireOp",EDGE,"E5");var subQ4=makeQuery(id+"F0.imprint","INTERSECT",VERTEX,{"disambiguationData":[OD(0.0)],"derivedFrom":[subQ3,subQ0]});Q28=makeQuery(id+"F0.imprint","IMPRINT",FACE,{"disambiguationData":[TD([[makeQuery(id+"F0.imprint","IMPRINT",EDGE,{"disambiguationData":[TD([[subQ4,-1.0]])],"derivedFrom":subQ3}),-1.0]])]});}
            var Q29;
            {var subQ1=sQuery(id+"F0.wireOp",EDGE,"E21.rect.top");var subQ5=sQuery(id+"F0.wireOp",EDGE,"E7");var subQ6=makeQuery(id+"F0.imprint","INTERSECT",VERTEX,{"disambiguationData":[OD(0.0)],"derivedFrom":[subQ5,subQ1]});Q29=makeQuery(id+"F0.imprint","IMPRINT",FACE,{"disambiguationData":[TD([[makeQuery(id+"F0.imprint","IMPRINT",EDGE,{"disambiguationData":[TD([[subQ6,-1.0]])],"derivedFrom":subQ5}),-1.0]])]});}
            var Q30;
            {var subQ3=sQuery(id+"F0.wireOp",EDGE,"E5");var subQ5=sQuery(id+"F0.wireOp",EDGE,"E21.rect.top");var subQ7=makeQuery(id+"F0.imprint","INTERSECT",VERTEX,{"disambiguationData":[OD(1.0)],"derivedFrom":[subQ3,subQ5]});Q30=makeQuery(id+"F0.imprint","IMPRINT",FACE,{"disambiguationData":[TD([[makeQuery(id+"F0.imprint","IMPRINT",EDGE,{"disambiguationData":[TD([[subQ7,1.0]])],"derivedFrom":subQ3}),-1.0]])]});}
            var Q31;
            {var subQ3=sQuery(id+"F0.wireOp",EDGE,"E4");var subQ10=makeQuery(id+"F0.imprint","INTERSECT",VERTEX,{"derivedFrom":[subQ3,sQuery(id+"F0.wireOp",EDGE,"E33")]});Q31=makeQuery(id+"F0.imprint","IMPRINT",FACE,{"disambiguationData":[TD([[makeQuery(id+"F0.imprint","IMPRINT",EDGE,{"disambiguationData":[TD([[subQ10,1.0]])],"derivedFrom":subQ3}),1.0]])]});}
            var Q32;
            {var subQ1=sQuery(id+"F0.wireOp",EDGE,"E21.rect.top");var subQ5=sQuery(id+"F0.wireOp",EDGE,"E4");var subQ7=makeQuery(id+"F0.imprint","INTERSECT",VERTEX,{"disambiguationData":[OD(0.0)],"derivedFrom":[subQ5,subQ1]});Q32=makeQuery(id+"F0.imprint","IMPRINT",FACE,{"disambiguationData":[TD([[makeQuery(id+"F0.imprint","IMPRINT",EDGE,{"disambiguationData":[TD([[subQ7,1.0]])],"derivedFrom":subQ5}),1.0]])]});}
            var Q33;
            {var subQ1=sQuery(id+"F0.wireOp",EDGE,"E21.rect.top");var subQ5=sQuery(id+"F0.wireOp",EDGE,"E7");var subQ6=makeQuery(id+"F0.imprint","INTERSECT",VERTEX,{"disambiguationData":[OD(1.0)],"derivedFrom":[subQ5,subQ1]});Q33=makeQuery(id+"F0.imprint","IMPRINT",FACE,{"disambiguationData":[TD([[makeQuery(id+"F0.imprint","IMPRINT",EDGE,{"disambiguationData":[TD([[subQ6,1.0]])],"derivedFrom":subQ5}),-1.0]])]});}
            extrude(context, id + "F3", {"entities" : qUnion([Q0, Q1, Q2, Q3, Q4, Q5, Q6, Q7, Q8, Q9, Q10, Q11, Q12, Q13, Q14, Q15, Q16, Q17, Q18, Q19, Q20, Q21, Q22, Q23, Q24, Q25, Q26, Q27, Q28, Q29, Q30, Q31, Q32, Q33]), "operationType" : NewBodyOperationType.ADD, "oppositeDirection" : true, "depth" : 2 * mm});
        }
        {
            var Q0;
            Q0=sQuery(id+"F0.wireOp",VERTEX,"E19");
            var Q1;
            Q1=sQuery(id+"F0.wireOp",VERTEX,"E16");
            var Q2;
            Q2=sQuery(id+"F0.wireOp",VERTEX,"E15");
            var Q3;
            Q3=sQuery(id+"F0.wireOp",VERTEX,"E13");
            var Q4;
            Q4=sQuery(id+"F0.wireOp",VERTEX,"E14");
            var Q5;
            Q5=sQuery(id+"F0.wireOp",VERTEX,"E20");
            var Q6;
            Q6=sQuery(id+"F0.wireOp",VERTEX,"E17");
            var Q7;
            Q7=sQuery(id+"F0.wireOp",VERTEX,"E18");
            var Q8;
            Q8=sQuery(id+"F0.wireOp",VERTEX,"E23");
            var Q9;
            Q9=sQuery(id+"F0.wireOp",VERTEX,"E22");
            var Q10;
            Q10=makeQuery(id+"F1.opExtrude","SWEPT_BODY",BODY,{"disambiguationData":[OSD([sQuery(id+"F0.wireOp",EDGE,"E0"),sQuery(id+"F0.wireOp",EDGE,"E1"),sQuery(id+"F0.wireOp",EDGE,"E4"),sQuery(id+"F0.wireOp",EDGE,"E5"),sQuery(id+"F0.wireOp",EDGE,"81c6133c-d079-48cb-b54b-84c7b39b5603"),sQuery(id+"F0.wireOp",EDGE,"59ee9ec7-6250-4acc-a49f-e67ea19ffa43"),sQuery(id+"F0.wireOp",EDGE,"8880f043-f8e5-4e1d-98a7-0d900bcb8cbe"),sQuery(id+"F0.wireOp",EDGE,"0e472ac9-51cb-4909-b52b-8bd739faff27"),sQuery(id+"F0.wireOp",EDGE,"E9"),sQuery(id+"F0.wireOp",EDGE,"E11.1.1"),sQuery(id+"F0.wireOp",EDGE,"E11.2.1"),sQuery(id+"F0.wireOp",EDGE,"E12.2.3.0"),sQuery(id+"F0.wireOp",EDGE,"E12.2.4.0"),sQuery(id+"F0.wireOp",EDGE,"E12.2.5.0"),sQuery(id+"F0.wireOp",EDGE,"E12.2.6.0"),sQuery(id+"F0.wireOp",EDGE,"E12.2.7.0"),sQuery(id+"F0.wireOp",EDGE,"166f7ea2-3097-4baf-8ef2-cccba6aa5040"),sQuery(id+"F0.wireOp",EDGE,"47d3ba70-d36f-4b99-a6e3-4a75f5d7ea0e"),sQuery(id+"F0.wireOp",EDGE,"c4b48481-116c-4d3a-8852-958f830b41e0"),sQuery(id+"F0.wireOp",EDGE,"0a7eceb2-8b87-48d4-a2db-88b3bf9defa5"),sQuery(id+"F0.wireOp",EDGE,"E21.rect.bottom"),sQuery(id+"F0.wireOp",EDGE,"E21.rect.top"),sQuery(id+"F0.wireOp",EDGE,"E25")])]});
            hole(context, id + "F4", {"style" : HoleStyle.SIMPLE, "holeDiameter" : 1.1 * mm, "endStyle" : HoleEndStyle.THROUGH, "locations" : qUnion([Q0, Q1, Q2, Q3, Q4, Q5, Q6, Q7, Q8, Q9]), "scope" : qUnion([Q10])});
        }
        {
            var Q0;
            Q0=sQuery(id+"F0.wireOp",VERTEX,"E23");
            var Q1;
            Q1=sQuery(id+"F0.wireOp",VERTEX,"E22");
            var Q2;
            Q2=sQuery(id+"F0.wireOp",VERTEX,"E18");
            var Q3;
            Q3=sQuery(id+"F0.wireOp",VERTEX,"E17");
            var Q4;
            Q4=sQuery(id+"F0.wireOp",VERTEX,"E20");
            var Q5;
            Q5=sQuery(id+"F0.wireOp",VERTEX,"E15");
            var Q6;
            Q6=sQuery(id+"F0.wireOp",VERTEX,"E16");
            var Q7;
            Q7=sQuery(id+"F0.wireOp",VERTEX,"E19");
            var Q8;
            Q8=sQuery(id+"F0.wireOp",VERTEX,"E13");
            var Q9;
            Q9=sQuery(id+"F0.wireOp",VERTEX,"E14");
            var Q10;
            Q10=makeQuery(id+"F1.opExtrude","SWEPT_BODY",BODY,{"disambiguationData":[OSD([sQuery(id+"F0.wireOp",EDGE,"E0"),sQuery(id+"F0.wireOp",EDGE,"E1"),sQuery(id+"F0.wireOp",EDGE,"E4"),sQuery(id+"F0.wireOp",EDGE,"E5"),sQuery(id+"F0.wireOp",EDGE,"81c6133c-d079-48cb-b54b-84c7b39b5603"),sQuery(id+"F0.wireOp",EDGE,"59ee9ec7-6250-4acc-a49f-e67ea19ffa43"),sQuery(id+"F0.wireOp",EDGE,"8880f043-f8e5-4e1d-98a7-0d900bcb8cbe"),sQuery(id+"F0.wireOp",EDGE,"0e472ac9-51cb-4909-b52b-8bd739faff27"),sQuery(id+"F0.wireOp",EDGE,"E9"),sQuery(id+"F0.wireOp",EDGE,"E11.1.1"),sQuery(id+"F0.wireOp",EDGE,"E11.2.1"),sQuery(id+"F0.wireOp",EDGE,"E12.2.3.0"),sQuery(id+"F0.wireOp",EDGE,"E12.2.4.0"),sQuery(id+"F0.wireOp",EDGE,"E12.2.5.0"),sQuery(id+"F0.wireOp",EDGE,"E12.2.6.0"),sQuery(id+"F0.wireOp",EDGE,"E12.2.7.0"),sQuery(id+"F0.wireOp",EDGE,"166f7ea2-3097-4baf-8ef2-cccba6aa5040"),sQuery(id+"F0.wireOp",EDGE,"47d3ba70-d36f-4b99-a6e3-4a75f5d7ea0e"),sQuery(id+"F0.wireOp",EDGE,"c4b48481-116c-4d3a-8852-958f830b41e0"),sQuery(id+"F0.wireOp",EDGE,"0a7eceb2-8b87-48d4-a2db-88b3bf9defa5"),sQuery(id+"F0.wireOp",EDGE,"E21.rect.bottom"),sQuery(id+"F0.wireOp",EDGE,"E21.rect.top"),sQuery(id+"F0.wireOp",EDGE,"E25")])]});
            hole(context, id + "F5", {"style" : HoleStyle.SIMPLE, "holeDiameter" : 1.1 * mm, "endStyle" : HoleEndStyle.THROUGH, "oppositeDirection" : true, "locations" : qUnion([Q0, Q1, Q2, Q3, Q4, Q5, Q6, Q7, Q8, Q9]), "scope" : qUnion([Q10])});
        }
        {
            var Q0;
            Q0=makeQuery(id+"F1.opExtrude","CAP_EDGE",EDGE,{"disambiguationData":[OSD([sQuery(id+"F0.wireOp",EDGE,"E30")])],"isStart":false});
            var Q1;
            Q1=makeQuery(id+"F1.opExtrude","CAP_EDGE",EDGE,{"disambiguationData":[OSD([sQuery(id+"F0.wireOp",EDGE,"E29")])],"isStart":false});
            var Q2;
            Q2=makeQuery(id+"F3.opExtrude","CAP_EDGE",EDGE,{"disambiguationData":[OSD([sQuery(id+"F0.wireOp",EDGE,"E30")])],"isStart":false});
            var Q3;
            {var subQ0=sQuery(id+"F0.wireOp",EDGE,"E4");Q3=makeQuery(id+"F1.opExtrude","CAP_EDGE",EDGE,{"disambiguationData":[OSD([subQ0]),TDD([makeQuery(id+"F0.imprint","IMPRINT",EDGE,{"disambiguationData":[TD([[makeQuery(id+"F0.imprint","INTERSECT",VERTEX,{"derivedFrom":[subQ0,sQuery(id+"F0.wireOp",EDGE,"E30")]}),-1.0]])],"derivedFrom":subQ0})])],"isStart":false});}
            var Q4;
            Q4=makeQuery(id+"F1.opExtrude","CAP_EDGE",EDGE,{"disambiguationData":[OSD([sQuery(id+"F0.wireOp",EDGE,"E34")])],"isStart":false});
            var Q5;
            {var subQ0=sQuery(id+"F0.wireOp",EDGE,"E0");Q5=makeQuery(id+"F1.opExtrude","CAP_EDGE",EDGE,{"disambiguationData":[OSD([subQ0]),TDD([makeQuery(id+"F0.imprint","IMPRINT",EDGE,{"disambiguationData":[TD([[makeQuery(id+"F0.imprint","INTERSECT",VERTEX,{"derivedFrom":[subQ0,sQuery(id+"F0.wireOp",EDGE,"E30")]}),-1.0]])],"derivedFrom":subQ0})])],"isStart":false});}
            var Q6;
            {var subQ0=sQuery(id+"F0.wireOp",EDGE,"E0");Q6=makeQuery(id+"F1.opExtrude","CAP_EDGE",EDGE,{"disambiguationData":[OSD([subQ0]),TDD([makeQuery(id+"F0.imprint","IMPRINT",EDGE,{"disambiguationData":[TD([[makeQuery(id+"F0.imprint","INTERSECT",VERTEX,{"derivedFrom":[subQ0,sQuery(id+"F0.wireOp",EDGE,"E29")]}),1.0]])],"derivedFrom":subQ0})])],"isStart":false});}
            var Q7;
            {var subQ0=sQuery(id+"F0.wireOp",EDGE,"E4");Q7=makeQuery(id+"F1.opExtrude","CAP_EDGE",EDGE,{"disambiguationData":[OSD([subQ0]),TDD([makeQuery(id+"F0.imprint","IMPRINT",EDGE,{"disambiguationData":[TD([[makeQuery(id+"F0.imprint","INTERSECT",VERTEX,{"derivedFrom":[subQ0,sQuery(id+"F0.wireOp",EDGE,"E29")]}),1.0]])],"derivedFrom":subQ0})])],"isStart":false});}
            var Q8;
            Q8=makeQuery(id+"F1.opExtrude","CAP_EDGE",EDGE,{"disambiguationData":[OSD([sQuery(id+"F0.wireOp",EDGE,"E32")])],"isStart":false});
            var Q9;
            {var subQ0=sQuery(id+"F0.wireOp",EDGE,"E0");Q9=makeQuery(id+"F3.opExtrude","CAP_EDGE",EDGE,{"disambiguationData":[OSD([subQ0]),TDD([makeQuery(id+"F0.imprint","IMPRINT",EDGE,{"disambiguationData":[TD([[makeQuery(id+"F0.imprint","INTERSECT",VERTEX,{"derivedFrom":[subQ0,sQuery(id+"F0.wireOp",EDGE,"E29")]}),1.0]])],"derivedFrom":subQ0})])],"isStart":false});}
            var Q10;
            {var subQ0=sQuery(id+"F0.wireOp",EDGE,"E0");Q10=makeQuery(id+"F3.opExtrude","CAP_EDGE",EDGE,{"disambiguationData":[OSD([subQ0]),TDD([makeQuery(id+"F0.imprint","IMPRINT",EDGE,{"disambiguationData":[TD([[makeQuery(id+"F0.imprint","INTERSECT",VERTEX,{"derivedFrom":[subQ0,sQuery(id+"F0.wireOp",EDGE,"E30")]}),-1.0]])],"derivedFrom":subQ0})])],"isStart":false});}
            var Q11;
            {var subQ0=sQuery(id+"F0.wireOp",EDGE,"E4");Q11=makeQuery(id+"F3.opExtrude","CAP_EDGE",EDGE,{"disambiguationData":[OSD([subQ0]),TDD([makeQuery(id+"F0.imprint","IMPRINT",EDGE,{"disambiguationData":[TD([[makeQuery(id+"F0.imprint","INTERSECT",VERTEX,{"derivedFrom":[subQ0,sQuery(id+"F0.wireOp",EDGE,"E30")]}),-1.0]])],"derivedFrom":subQ0})])],"isStart":false});}
            var Q12;
            {var subQ0=sQuery(id+"F0.wireOp",EDGE,"E4");Q12=makeQuery(id+"F3.opExtrude","CAP_EDGE",EDGE,{"disambiguationData":[OSD([subQ0]),TDD([makeQuery(id+"F0.imprint","IMPRINT",EDGE,{"disambiguationData":[TD([[makeQuery(id+"F0.imprint","INTERSECT",VERTEX,{"derivedFrom":[subQ0,sQuery(id+"F0.wireOp",EDGE,"E29")]}),1.0]])],"derivedFrom":subQ0})])],"isStart":false});}
            var Q13;
            Q13=makeQuery(id+"F3.opExtrude","CAP_EDGE",EDGE,{"disambiguationData":[OSD([sQuery(id+"F0.wireOp",EDGE,"E29")])],"isStart":false});
            var Q14;
            Q14=makeQuery(id+"F3.opExtrude","CAP_EDGE",EDGE,{"disambiguationData":[OSD([sQuery(id+"F0.wireOp",EDGE,"E32")])],"isStart":false});
            var Q15;
            {var subQ0=sQuery(id+"F0.wireOp",EDGE,"E4");Q15=makeQuery(id+"F3.opExtrude","CAP_EDGE",EDGE,{"disambiguationData":[OSD([subQ0]),TDD([makeQuery(id+"F0.imprint","IMPRINT",EDGE,{"disambiguationData":[TD([[makeQuery(id+"F0.imprint","INTERSECT",VERTEX,{"derivedFrom":[subQ0,sQuery(id+"F0.wireOp",EDGE,"E33")]}),-1.0]])],"derivedFrom":subQ0})])],"isStart":false});}
            var Q16;
            {var subQ0=sQuery(id+"F0.wireOp",EDGE,"E4");Q16=makeQuery(id+"F3.opExtrude","CAP_EDGE",EDGE,{"disambiguationData":[OSD([subQ0]),TDD([makeQuery(id+"F0.imprint","IMPRINT",EDGE,{"disambiguationData":[TD([[makeQuery(id+"F0.imprint","INTERSECT",VERTEX,{"derivedFrom":[subQ0,sQuery(id+"F0.wireOp",EDGE,"E31")]}),1.0]])],"derivedFrom":subQ0})])],"isStart":false});}
            var Q17;
            Q17=makeQuery(id+"F3.opExtrude","CAP_EDGE",EDGE,{"disambiguationData":[OSD([sQuery(id+"F0.wireOp",EDGE,"E36")])],"isStart":false});
            var Q18;
            Q18=makeQuery(id+"F3.opExtrude","CAP_EDGE",EDGE,{"disambiguationData":[OSD([sQuery(id+"F0.wireOp",EDGE,"E35")])],"isStart":false});
            var Q19;
            {var subQ0=sQuery(id+"F0.wireOp",EDGE,"E0");Q19=makeQuery(id+"F3.opExtrude","CAP_EDGE",EDGE,{"disambiguationData":[OSD([subQ0]),TDD([makeQuery(id+"F0.imprint","IMPRINT",EDGE,{"disambiguationData":[TD([[makeQuery(id+"F0.imprint","INTERSECT",VERTEX,{"derivedFrom":[subQ0,sQuery(id+"F0.wireOp",EDGE,"E33")]}),-1.0]])],"derivedFrom":subQ0})])],"isStart":false});}
            var Q20;
            {var subQ0=sQuery(id+"F0.wireOp",EDGE,"E0");Q20=makeQuery(id+"F1.opExtrude","CAP_EDGE",EDGE,{"disambiguationData":[OSD([subQ0]),TDD([makeQuery(id+"F0.imprint","IMPRINT",EDGE,{"disambiguationData":[TD([[makeQuery(id+"F0.imprint","INTERSECT",VERTEX,{"derivedFrom":[subQ0,sQuery(id+"F0.wireOp",EDGE,"E33")]}),-1.0]])],"derivedFrom":subQ0})])],"isStart":false});}
            var Q21;
            Q21=makeQuery(id+"F3.opExtrude","CAP_EDGE",EDGE,{"disambiguationData":[OSD([sQuery(id+"F0.wireOp",EDGE,"E33")])],"isStart":false});
            var Q22;
            Q22=makeQuery(id+"F3.opExtrude","CAP_EDGE",EDGE,{"disambiguationData":[OSD([sQuery(id+"F0.wireOp",EDGE,"E31")])],"isStart":false});
            var Q23;
            Q23=makeQuery(id+"F1.opExtrude","CAP_EDGE",EDGE,{"disambiguationData":[OSD([sQuery(id+"F0.wireOp",EDGE,"E36")])],"isStart":false});
            var Q24;
            {var subQ0=sQuery(id+"F0.wireOp",EDGE,"E0");Q24=makeQuery(id+"F3.opExtrude","CAP_EDGE",EDGE,{"disambiguationData":[OSD([subQ0]),TDD([makeQuery(id+"F0.imprint","IMPRINT",EDGE,{"disambiguationData":[TD([[makeQuery(id+"F0.imprint","INTERSECT",VERTEX,{"derivedFrom":[subQ0,sQuery(id+"F0.wireOp",EDGE,"E31")]}),1.0]])],"derivedFrom":subQ0})])],"isStart":false});}
            var Q25;
            {var subQ0=sQuery(id+"F0.wireOp",EDGE,"E4");Q25=makeQuery(id+"F1.opExtrude","CAP_EDGE",EDGE,{"disambiguationData":[OSD([subQ0]),TDD([makeQuery(id+"F0.imprint","IMPRINT",EDGE,{"disambiguationData":[TD([[makeQuery(id+"F0.imprint","INTERSECT",VERTEX,{"derivedFrom":[subQ0,sQuery(id+"F0.wireOp",EDGE,"E31")]}),1.0]])],"derivedFrom":subQ0})])],"isStart":false});}
            var Q26;
            {var subQ0=sQuery(id+"F0.wireOp",EDGE,"E0");Q26=makeQuery(id+"F1.opExtrude","CAP_EDGE",EDGE,{"disambiguationData":[OSD([subQ0]),TDD([makeQuery(id+"F0.imprint","IMPRINT",EDGE,{"disambiguationData":[TD([[makeQuery(id+"F0.imprint","INTERSECT",VERTEX,{"derivedFrom":[subQ0,sQuery(id+"F0.wireOp",EDGE,"E31")]}),1.0]])],"derivedFrom":subQ0})])],"isStart":false});}
            var Q27;
            Q27=makeQuery(id+"F1.opExtrude","CAP_EDGE",EDGE,{"disambiguationData":[OSD([sQuery(id+"F0.wireOp",EDGE,"E31")])],"isStart":false});
            var Q28;
            Q28=makeQuery(id+"F1.opExtrude","CAP_EDGE",EDGE,{"disambiguationData":[OSD([sQuery(id+"F0.wireOp",EDGE,"E33")])],"isStart":false});
            var Q29;
            Q29=makeQuery(id+"F1.opExtrude","CAP_EDGE",EDGE,{"disambiguationData":[OSD([sQuery(id+"F0.wireOp",EDGE,"E35")])],"isStart":false});
            var Q30;
            {var subQ0=sQuery(id+"F0.wireOp",EDGE,"E4");Q30=makeQuery(id+"F1.opExtrude","CAP_EDGE",EDGE,{"disambiguationData":[OSD([subQ0]),TDD([makeQuery(id+"F0.imprint","IMPRINT",EDGE,{"disambiguationData":[TD([[makeQuery(id+"F0.imprint","INTERSECT",VERTEX,{"derivedFrom":[subQ0,sQuery(id+"F0.wireOp",EDGE,"E33")]}),-1.0]])],"derivedFrom":subQ0})])],"isStart":false});}
            fillet(context, id + "F6", {"entities" : qUnion([Q0, Q1, Q2, Q3, Q4, Q5, Q6, Q7, Q8, Q9, Q10, Q11, Q12, Q13, Q14, Q15, Q16, Q17, Q18, Q19, Q20, Q21, Q22, Q23, Q24, Q25, Q26, Q27, Q28, Q29, Q30]), "radius" : 1.5 * mm, "tangentPropagation" : true, "allowEdgeOverflow" : false});
        }
    });
